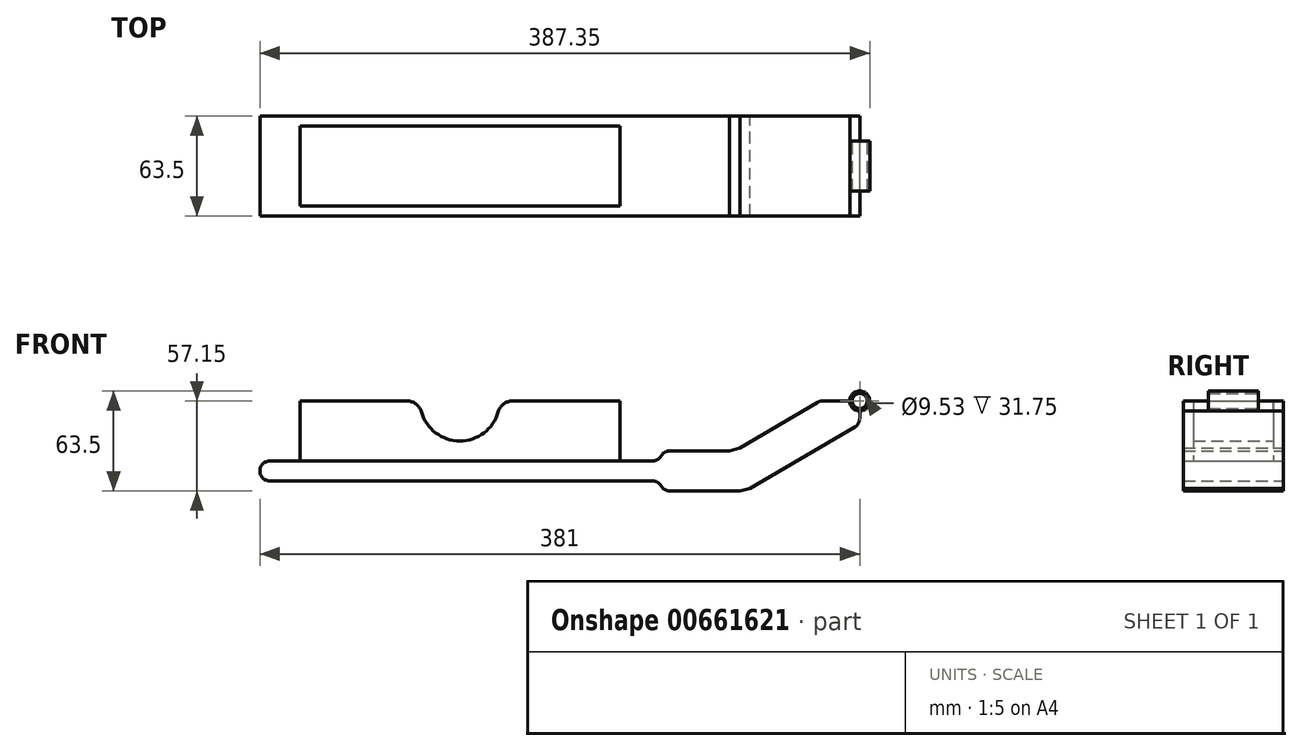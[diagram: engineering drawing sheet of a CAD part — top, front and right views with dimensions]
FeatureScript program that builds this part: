
annotation { "Feature Type Name" : "Feature", "Feature Type Description" : "" }
export const myFeature = defineFeature(function(context is Context, id is Id, definition is map)
    precondition{}
    {
        {
            var Q0;
            Q0=qCreatedBy(makeId("Front.planeOp"),FACE);
            var sketch = newSketch(context, id + "F0", { "sketchPlane" : qUnion([Q0])});
            skLineSegment(sketch, "E0", {"start": v(0, 0) * mm, "end": v(-4.76, 0) * mm});
            skCircle(sketch, "E1", {"center": v(0, 0) * mm, "radius": 4.76 * mm});
            skArc(sketch, "E2", {"start": v(0, -6.35) * mm, "mid": v(4.5, 4.5) * mm, "end": v(-6.35, 0) * mm});
            skLineSegment(sketch, "E3", {"start": v(-355.6, 0) * mm, "end": v(-355.6, -38.1) * mm});
            skLineSegment(sketch, "E4", {"start": v(-152.4, 0) * mm, "end": v(-152.4, -38.1) * mm});
            skLineSegment(sketch, "E5", {"start": v(-152.4, -38.1) * mm, "end": v(-355.6, -38.1) * mm});
            skLineSegment(sketch, "E6", {"start": v(-355.6, -38.1) * mm, "end": v(-374.65, -38.1) * mm});
            skLineSegment(sketch, "E7", {"start": v(-381, -44.45) * mm, "end": v(-381, -44.45) * mm});
            skLineSegment(sketch, "E8", {"start": v(-374.65, -50.8) * mm, "end": v(-131.65, -50.8) * mm});
            skLineSegment(sketch, "E9", {"start": v(-131.65, -38.1) * mm, "end": v(-152.4, -38.1) * mm});
            skLineSegment(sketch, "E10", {"start": v(0, -6.35) * mm, "end": v(0, -11.06) * mm});
            skPoint(sketch, "E10.endSnap0", {"position": v(-127, -44.45) * mm});
            skLineSegment(sketch, "E11.0", {"start": v(-76.2, -57.15) * mm, "end": v(-120.65, -57.15) * mm});
            skLineSegment(sketch, "E12.0", {"start": v(-82.6, -31.75) * mm, "end": v(-120.65, -31.75) * mm});
            skLineSegment(sketch, "E13.0", {"start": v(-76.2, -29.75) * mm, "end": v(-26.69, -0.87) * mm});
            skLineSegment(sketch, "E14.0", {"start": v(-69.8, -55.42) * mm, "end": v(-3.15, -16.54) * mm});
            skLineSegment(sketch, "E15", {"start": v(-127, -38.1) * mm, "end": v(-127, -38.1) * mm});
            skLineSegment(sketch, "E16", {"start": v(-127, -50.8) * mm, "end": v(-127, -50.8) * mm});
            skLineSegment(sketch, "E17", {"start": v(-76.2, -57.15) * mm, "end": v(-69.8, -55.42) * mm});
            skLineSegment(sketch, "E18", {"start": v(-82.6, -31.75) * mm, "end": v(-76.2, -29.75) * mm});
            skPoint(sketch, "E19.orphan", {"position": v(-82.6, -33.48) * mm});
            skPoint(sketch, "E20.orphan", {"position": v(-76.2, -31.75) * mm});
            skPoint(sketch, "E21.orphan", {"position": v(0, -44.45) * mm});
            skPoint(sketch, "E22.visualSharp", {"position": v(-127, -31.75) * mm});
            skArc(sketch, "E22.filletArc", {"start": v(-120.65, -31.75) * mm, "mid": v(-123.83, -32.6) * mm, "end": v(-126.15, -34.92) * mm});
            skPoint(sketch, "E23.visualSharp", {"position": v(-127, -57.15) * mm});
            skArc(sketch, "E23.filletArc", {"start": v(-126.15, -53.98) * mm, "mid": v(-123.82, -56.3) * mm, "end": v(-120.65, -57.15) * mm});
            skPoint(sketch, "E24.visualSharp", {"position": v(-127, -38.1) * mm});
            skArc(sketch, "E24.filletArc", {"start": v(-131.65, -38.1) * mm, "mid": v(-128.47, -37.25) * mm, "end": v(-126.15, -34.93) * mm});
            skPoint(sketch, "E25.visualSharp", {"position": v(-127, -50.8) * mm});
            skArc(sketch, "E25.filletArc", {"start": v(-126.15, -53.98) * mm, "mid": v(-128.47, -51.65) * mm, "end": v(-131.65, -50.8) * mm});
            skPoint(sketch, "E26.visualSharp", {"position": v(-381, -50.8) * mm});
            skArc(sketch, "E26.filletArc", {"start": v(-381, -44.45) * mm, "mid": v(-379.14, -48.94) * mm, "end": v(-374.65, -50.8) * mm});
            skPoint(sketch, "E27.visualSharp", {"position": v(-381, -38.1) * mm});
            skArc(sketch, "E27.filletArc", {"start": v(-374.65, -38.1) * mm, "mid": v(-379.14, -39.96) * mm, "end": v(-381, -44.45) * mm});
            skPoint(sketch, "E28.visualSharp", {"position": v(0, -14.7) * mm});
            skArc(sketch, "E28.filletArc", {"start": v(-3.15, -16.54) * mm, "mid": v(-0.84, -14.22) * mm, "end": v(0, -11.06) * mm});
            skPoint(sketch, "E29.visualSharp", {"position": v(-25.2, 0) * mm});
            skArc(sketch, "E29.filletArc", {"start": v(-23.49, 0) * mm, "mid": v(-25.15, -0.22) * mm, "end": v(-26.69, -0.87) * mm});
            skLineSegment(sketch, "E30.trimOffspring", {"start": v(-6.35, 0) * mm, "end": v(-23.49, 0) * mm});
            skLineSegment(sketch, "E31.trimOffspring", {"start": v(-6.35, 0) * mm, "end": v(-25.2, 0) * mm});
            skLineSegment(sketch, "E32.trimOffspring", {"start": v(-152.4, 0) * mm, "end": v(-220.4, 0) * mm});
            skPoint(sketch, "E33.start.orphan", {"position": v(-381, 0) * mm});
            skArc(sketch, "E34", {"start": v(-278.44, -6.93) * mm, "mid": v(-254, -25.4) * mm, "end": v(-229.56, -6.93) * mm});
            skLineSegment(sketch, "E35.trimOffspring", {"start": v(-287.6, 0) * mm, "end": v(-355.6, 0) * mm});
            skPoint(sketch, "E36.visualSharp", {"position": v(-279.4, 0) * mm});
            skArc(sketch, "E36.filletArc", {"start": v(-278.44, -6.93) * mm, "mid": v(-281.86, -1.93) * mm, "end": v(-287.6, 0) * mm});
            skPoint(sketch, "E37.visualSharp", {"position": v(-228.6, 0) * mm});
            skArc(sketch, "E37.filletArc", {"start": v(-220.4, 0) * mm, "mid": v(-226.14, -1.93) * mm, "end": v(-229.56, -6.93) * mm});
            skSolve(sketch);
        }
        {
            var Q0;
            Q0=makeQuery(id+"F0.imprint","IMPRINT",FACE,{"disambiguationData":[TD([[makeQuery(id+"F0.imprint","IMPRINT",EDGE,{"derivedFrom":sQuery(id+"F0.wireOp",EDGE,"E1")}),-1.0]])]});
            extrude(context, id + "F1", {"entities" : qUnion([Q0]), "depth" : 31.75 * mm, "offsetDistance" : 25.4 * mm, "hasSecondDirection" : true, "secondDirectionOppositeDirection" : true, "secondDirectionDepth" : 31.75 * mm});
        }
        {
            var Q0;
            Q0=qSketchRegion(id+"F0",true);
            extrude(context, id + "F2", {"entities" : qUnion([Q0]), "operationType" : NewBodyOperationType.ADD, "depth" : 25.4 * mm, "offsetDistance" : 25.4 * mm, "hasSecondDirection" : true, "secondDirectionOppositeDirection" : true, "secondDirectionDepth" : 25.4 * mm});
        }
        {
            var Q0;
            Q0=makeQuery(id+"F1.opExtrude","CAP_FACE",FACE,{"disambiguationData":[OSD([sQuery(id+"F0.wireOp",EDGE,"E1"),sQuery(id+"F0.wireOp",EDGE,"E2"),sQuery(id+"F0.wireOp",EDGE,"E5"),sQuery(id+"F0.wireOp",EDGE,"E6"),sQuery(id+"F0.wireOp",EDGE,"E8"),sQuery(id+"F0.wireOp",EDGE,"E9"),sQuery(id+"F0.wireOp",EDGE,"E10"),sQuery(id+"F0.wireOp",EDGE,"E11.0"),sQuery(id+"F0.wireOp",EDGE,"E12.0"),sQuery(id+"F0.wireOp",EDGE,"E13.0"),sQuery(id+"F0.wireOp",EDGE,"E14.0"),sQuery(id+"F0.wireOp",EDGE,"E17"),sQuery(id+"F0.wireOp",EDGE,"E18"),sQuery(id+"F0.wireOp",EDGE,"E22.filletArc"),sQuery(id+"F0.wireOp",EDGE,"E23.filletArc"),sQuery(id+"F0.wireOp",EDGE,"E24.filletArc"),sQuery(id+"F0.wireOp",EDGE,"E25.filletArc"),sQuery(id+"F0.wireOp",EDGE,"E26.filletArc"),sQuery(id+"F0.wireOp",EDGE,"E27.filletArc"),sQuery(id+"F0.wireOp",EDGE,"E28.filletArc"),sQuery(id+"F0.wireOp",EDGE,"E29.filletArc"),sQuery(id+"F0.wireOp",EDGE,"E31.trimOffspring")])],"isStart":false});
            var sketch = newSketch(context, id + "F3", { "sketchPlane" : qUnion([Q0])});
            skCircle(sketch, "E38", {"center": v(0, 0) * mm, "radius": 6.35 * mm});
            skSolve(sketch);
        }
        {
            var Q0;
            Q0 = qSketchRegion(id + "F3", true);
            extrude(context, id + "F4", {"entities" : qUnion([Q0]), "operationType" : NewBodyOperationType.REMOVE, "oppositeDirection" : true, "depth" : 15.88 * mm, "offsetDistance" : 25.4 * mm});
        }
        {
            var Q0;
            Q0=makeQuery(id+"F1.opExtrude","CAP_FACE",FACE,{"disambiguationData":[OSD([sQuery(id+"F0.wireOp",EDGE,"E1"),sQuery(id+"F0.wireOp",EDGE,"E2"),sQuery(id+"F0.wireOp",EDGE,"E5"),sQuery(id+"F0.wireOp",EDGE,"E6"),sQuery(id+"F0.wireOp",EDGE,"E8"),sQuery(id+"F0.wireOp",EDGE,"E9"),sQuery(id+"F0.wireOp",EDGE,"E10"),sQuery(id+"F0.wireOp",EDGE,"E11.0"),sQuery(id+"F0.wireOp",EDGE,"E12.0"),sQuery(id+"F0.wireOp",EDGE,"E13.0"),sQuery(id+"F0.wireOp",EDGE,"E14.0"),sQuery(id+"F0.wireOp",EDGE,"E17"),sQuery(id+"F0.wireOp",EDGE,"E18"),sQuery(id+"F0.wireOp",EDGE,"E22.filletArc"),sQuery(id+"F0.wireOp",EDGE,"E23.filletArc"),sQuery(id+"F0.wireOp",EDGE,"E24.filletArc"),sQuery(id+"F0.wireOp",EDGE,"E25.filletArc"),sQuery(id+"F0.wireOp",EDGE,"E26.filletArc"),sQuery(id+"F0.wireOp",EDGE,"E27.filletArc"),sQuery(id+"F0.wireOp",EDGE,"E28.filletArc"),sQuery(id+"F0.wireOp",EDGE,"E29.filletArc"),sQuery(id+"F0.wireOp",EDGE,"E31.trimOffspring")])],"isStart":true});
            var sketch = newSketch(context, id + "F5", { "sketchPlane" : qUnion([Q0])});
            skCircle(sketch, "E39", {"center": v(0, 0) * mm, "radius": 6.35 * mm});
            skSolve(sketch);
        }
        {
            var Q0;
            Q0 = qSketchRegion(id + "F5", true);
            extrude(context, id + "F6", {"entities" : qUnion([Q0]), "operationType" : NewBodyOperationType.REMOVE, "oppositeDirection" : true, "depth" : 15.88 * mm, "offsetDistance" : 25.4 * mm});
        }
    });
